# Revit family: Hitachi_RAS-25YHA5_RAS-35YHA6_1116
name_source: partatom
category: Mechanical Equipment
revit_build: Autodesk Revit 2013 (Build: 20120221_2030(x64)
units: mm (PartAtom-declared; Revit-internal decimal feet)

## types (2) — shared parameters
Depth = 218 mm  [stored 0.715223 ft]
Energy Star = Yes
Height = 280 mm  [stored 0.918635 ft]
Manufacturer = Hitachi
Pip Connection Size - Liquid = 6.40 mm
Pipe Connection Size - Gas = 9.50 mm
Pipe Height (max.) = 10m
Pipe Length (min./max.) = 2m to 30m
URL = www.temperzone.biz
Weight (kg) = 7.5
Width = 780 mm  [stored 2.55906 ft]

## per-type parameters (varying)
| type | Cooling Capacity | Cooling Range (kW) | Description | Heating Capacity | Heating Range (kW) | Model - Outdoor |
| RAS-35YHA6 | 4 kW | 1.1 kW to 4.2 kW | Hitachi Wall Mounted 3.5kW Heatpump RAS-35YHA6 | 4 kW | 1.1 kW to 5.5 kW | RAC-35YHA6 |
| RAS-25YHA5 | 3 kW | 1.0 kW to 3.2 kW | Hitachi Wall Mounted 2.5kW Heatpump RAS-25YHA5 | 3 kW | 1.0 kW to 4.4 kW | RAC-25YHA5 |

note: column(s) folded — value = type name in every type: Model

note: [stored X ft] marks values corroborated as IEEE doubles in the binary element streams (Revit-internal decimal feet)

## geometry (parser evidence)
native form markers: Blend x4, Sweep x3
no freeform markers — native parametric forms only
